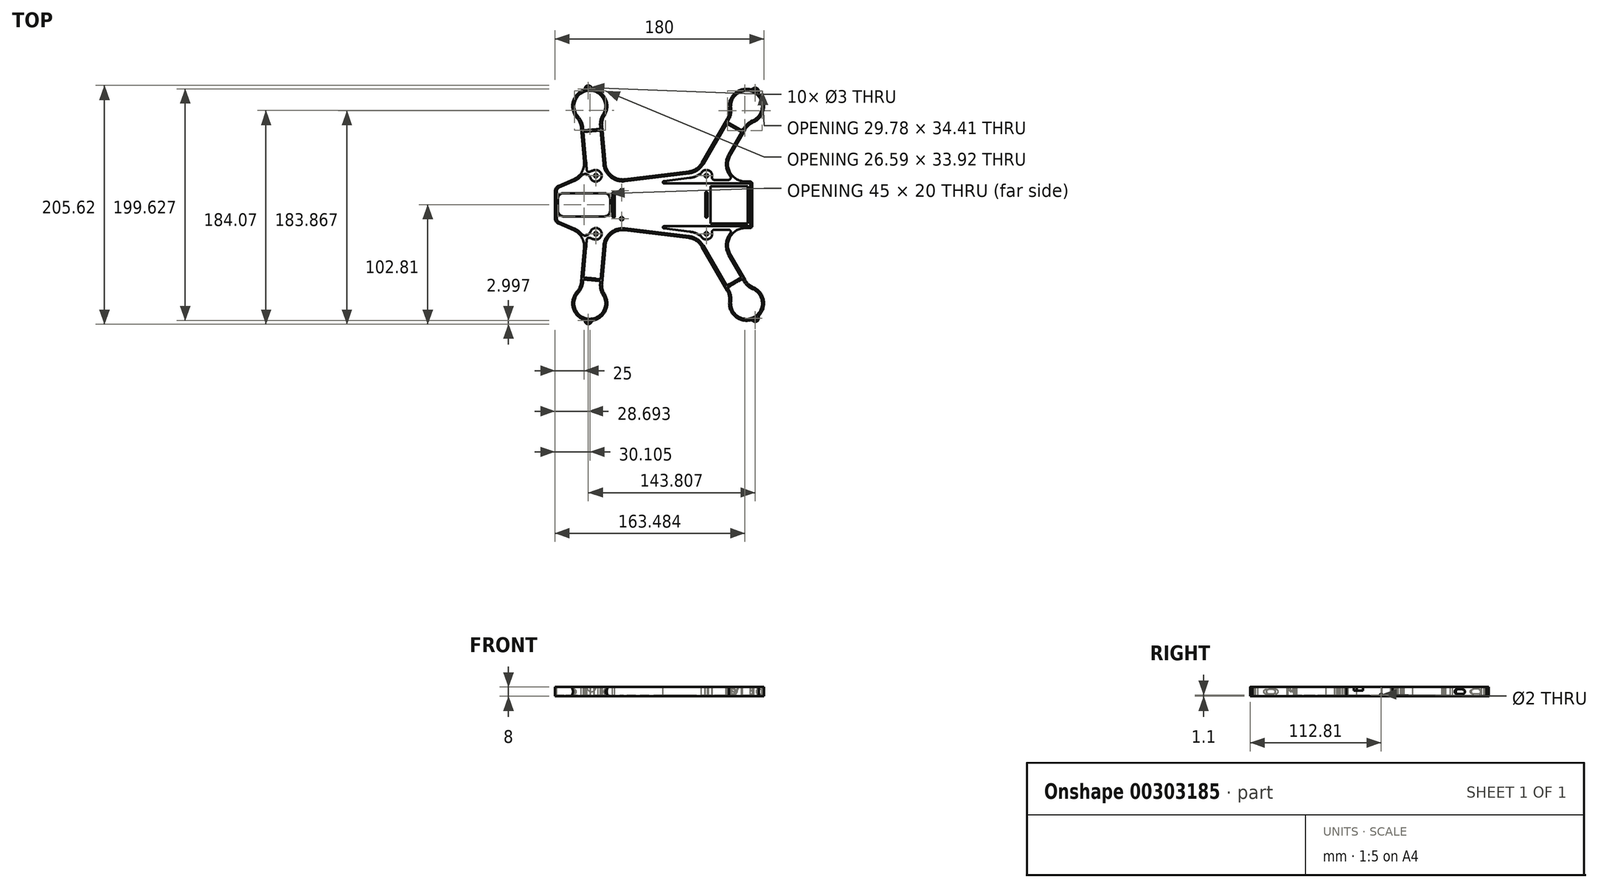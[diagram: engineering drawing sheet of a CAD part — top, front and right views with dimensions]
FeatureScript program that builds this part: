
annotation { "Feature Type Name" : "Feature", "Feature Type Description" : "" }
export const myFeature = defineFeature(function(context is Context, id is Id, definition is map)
    precondition{}
    {
        {
            var Q0;
            Q0=qCreatedBy(makeId("Top.planeOp"),FACE);
            var sketch = newSketch(context, id + "F0", { "sketchPlane" : qUnion([Q0])});
            skLineSegment(sketch, "E0", {"start": v(-85, 0) * mm, "end": v(85, 0) * mm, "construction": true});
            skLineSegment(sketch, "E1", {"start": v(-47.57, 0) * mm, "end": v(-55, -84.87) * mm, "construction": true});
            skLineSegment(sketch, "E2", {"start": v(31, 0) * mm, "end": v(80, -84.87) * mm, "construction": true});
            skArc(sketch, "E3", {"start": v(-66.17, -74.86) * mm, "mid": v(-69.65, -88.1) * mm, "end": v(-60.9, -98.66) * mm});
            skArc(sketch, "E4", {"start": v(65.1, -83.08) * mm, "mid": v(69.86, -95.92) * mm, "end": v(83.07, -99.55) * mm});
            skLineSegment(sketch, "E5", {"start": v(-85, 0) * mm, "end": v(-85, -11.72) * mm});
            skLineSegment(sketch, "E6", {"start": v(-59.85, -37.08) * mm, "end": v(-62.4, -66.15) * mm});
            skLineSegment(sketch, "E7", {"start": v(-44.47, -67.72) * mm, "end": v(-41.64, -35.47) * mm});
            skLineSegment(sketch, "E8", {"start": v(-24.87, -21.9) * mm, "end": v(30.26, -28.66) * mm});
            skLineSegment(sketch, "E9", {"start": v(41.42, -36.05) * mm, "end": v(63.2, -73.78) * mm});
            skLineSegment(sketch, "E10", {"start": v(78.8, -64.78) * mm, "end": v(65.93, -42.5) * mm});
            skLineSegment(sketch, "E11", {"start": v(78.92, -20) * mm, "end": v(83, -20) * mm});
            skLineSegment(sketch, "E12", {"start": v(85, -18) * mm, "end": v(85, 0) * mm});
            skPoint(sketch, "E13.visualSharp", {"position": v(-40.3, -20) * mm});
            skArc(sketch, "E13.filletArc", {"start": v(-24.87, -21.9) * mm, "mid": v(-36.14, -25.12) * mm, "end": v(-41.64, -35.47) * mm});
            skPoint(sketch, "E14.visualSharp", {"position": v(52.94, -20) * mm});
            skPoint(sketch, "E15.visualSharp", {"position": v(37.68, -29.57) * mm});
            skArc(sketch, "E15.filletArc", {"start": v(41.42, -36.05) * mm, "mid": v(36.71, -31.04) * mm, "end": v(30.26, -28.66) * mm});
            skPoint(sketch, "E16.visualSharp", {"position": v(85, -20) * mm});
            skArc(sketch, "E16.filletArc", {"start": v(83, -20) * mm, "mid": v(84.41, -19.41) * mm, "end": v(85, -18) * mm});
            skArc(sketch, "E17.filletArc", {"start": v(78.92, -20) * mm, "mid": v(65.93, -27.5) * mm, "end": v(65.93, -42.5) * mm});
            skPoint(sketch, "E18.visualSharp", {"position": v(-62.92, -72.13) * mm});
            skArc(sketch, "E18.filletArc", {"start": v(-66.17, -74.86) * mm, "mid": v(-63.58, -70.81) * mm, "end": v(-62.4, -66.15) * mm});
            skPoint(sketch, "E19.visualSharp", {"position": v(-44.99, -73.7) * mm});
            skArc(sketch, "E19.filletArc", {"start": v(-44.47, -67.72) * mm, "mid": v(-44.11, -72.52) * mm, "end": v(-42.26, -76.95) * mm});
            skArc(sketch, "E20.filletArc", {"start": v(65.1, -83.08) * mm, "mid": v(64.91, -78.27) * mm, "end": v(63.2, -73.78) * mm});
            skPoint(sketch, "E21.visualSharp", {"position": v(81.8, -69.98) * mm});
            skArc(sketch, "E21.filletArc", {"start": v(78.8, -64.78) * mm, "mid": v(81.83, -68.5) * mm, "end": v(85.9, -71.08) * mm});
            skLineSegment(sketch, "E22", {"start": v(-81.99, -16.3) * mm, "end": v(-68.83, -22) * mm});
            skPoint(sketch, "E23.visualSharp", {"position": v(-85, -15) * mm});
            skArc(sketch, "E23.filletArc", {"start": v(-85, -11.72) * mm, "mid": v(-84.18, -14.46) * mm, "end": v(-81.99, -16.3) * mm});
            skPoint(sketch, "E24.visualSharp", {"position": v(-58.91, -26.3) * mm});
            skArc(sketch, "E25.filletArc", {"start": v(-59.85, -37.08) * mm, "mid": v(-61.9, -28.1) * mm, "end": v(-68.83, -22) * mm});
            skLineSegment(sketch, "E26", {"start": v(78.92, -20) * mm, "end": v(-122.08, -20) * mm, "construction": true});
            skLineSegment(sketch, "E27", {"start": v(-55, -84.87) * mm, "end": v(-57.29, -111.02) * mm, "construction": true});
            skLineSegment(sketch, "E28", {"start": v(80, -84.87) * mm, "end": v(94.45, -109.9) * mm, "construction": true});
            skArc(sketch, "E29.trimOffspring", {"start": v(-51.58, -99.47) * mm, "mid": v(-41.14, -90.6) * mm, "end": v(-42.26, -76.95) * mm});
            skCircle(sketch, "E30", {"center": v(87.5, -97.86) * mm, "radius": 1.5 * mm});
            skArc(sketch, "E31", {"start": v(85.6, -100.18) * mm, "mid": v(89, -100.46) * mm, "end": v(90.46, -97.37) * mm});
            skArc(sketch, "E32.trimOffspring", {"start": v(91.18, -94.87) * mm, "mid": v(94.64, -81.62) * mm, "end": v(85.9, -71.08) * mm});
            skPoint(sketch, "E33.visualSharp", {"position": v(89.94, -96.1) * mm});
            skArc(sketch, "E33.filletArc", {"start": v(91.18, -94.87) * mm, "mid": v(90.54, -96.04) * mm, "end": v(90.46, -97.37) * mm});
            skPoint(sketch, "E34.visualSharp", {"position": v(84.76, -99.1) * mm});
            skArc(sketch, "E35.filletArc", {"start": v(85.6, -100.18) * mm, "mid": v(84.4, -99.58) * mm, "end": v(83.07, -99.55) * mm});
            skCircle(sketch, "E36", {"center": v(-49.76, -25) * mm, "radius": 1.5 * mm});
            skCircle(sketch, "E37", {"center": v(45.43, -25) * mm, "radius": 1.5 * mm});
            skCircle(sketch, "E38", {"center": v(-56.3, -99.81) * mm, "radius": 1.5 * mm});
            skArc(sketch, "E39", {"start": v(-59.2, -100.61) * mm, "mid": v(-56.57, -102.8) * mm, "end": v(-53.6, -101.1) * mm});
            skPoint(sketch, "E40.visualSharp", {"position": v(-53.3, -99.77) * mm});
            skArc(sketch, "E40.filletArc", {"start": v(-51.58, -99.47) * mm, "mid": v(-52.77, -100.06) * mm, "end": v(-53.6, -101.1) * mm});
            skPoint(sketch, "E41.visualSharp", {"position": v(-59.25, -99.25) * mm});
            skArc(sketch, "E41.filletArc", {"start": v(-59.2, -100.61) * mm, "mid": v(-59.83, -99.44) * mm, "end": v(-60.9, -98.66) * mm});
            skLineSegment(sketch, "E42", {"start": v(-55, -84.87) * mm, "end": v(80, -84.87) * mm, "construction": true});
            skLineSegment(sketch, "E43", {"start": v(85, -15) * mm, "end": v(-122.38, -15) * mm, "construction": true});
            skLineSegment(sketch, "E44.2", {"start": v(78.92, -18.4) * mm, "end": v(80, -18.4) * mm});
            skLineSegment(sketch, "E44.4", {"start": v(77.4, -65.58) * mm, "end": v(76.4, -63.85) * mm});
            skArc(sketch, "E44.5", {"start": v(-51.94, -97.92) * mm, "mid": v(-42.62, -90) * mm, "end": v(-43.62, -77.8) * mm});
            skArc(sketch, "E44.8", {"start": v(-64.98, -75.93) * mm, "mid": v(-66.53, -91.7) * mm, "end": v(-51.94, -97.92) * mm});
            skArc(sketch, "E44.9", {"start": v(-64.98, -75.93) * mm, "mid": v(-62.1, -71.45) * mm, "end": v(-60.8, -66.3) * mm});
            skArc(sketch, "E44.15", {"start": v(-46.06, -67.58) * mm, "mid": v(-45.67, -72.89) * mm, "end": v(-43.62, -77.8) * mm});
            skLineSegment(sketch, "E44.16", {"start": v(-46.06, -67.58) * mm, "end": v(-45.89, -65.6) * mm});
            skLineSegment(sketch, "E44.19", {"start": v(30.45, -27.07) * mm, "end": v(30.45, -27.07) * mm});
            skArc(sketch, "E44.21", {"start": v(66.7, -83.27) * mm, "mid": v(66.48, -77.95) * mm, "end": v(64.6, -72.98) * mm});
            skArc(sketch, "E44.22", {"start": v(66.7, -83.27) * mm, "mid": v(74.48, -97.08) * mm, "end": v(89.99, -93.8) * mm});
            skArc(sketch, "E44.25", {"start": v(89.99, -93.8) * mm, "mid": v(93.08, -81.96) * mm, "end": v(85.26, -72.55) * mm});
            skArc(sketch, "E44.26", {"start": v(77.4, -65.58) * mm, "mid": v(80.77, -69.7) * mm, "end": v(85.26, -72.55) * mm});
            skPoint(sketch, "E45.visualSharp", {"position": v(-2, -22.69) * mm});
            skPoint(sketch, "E46.visualSharp", {"position": v(2, -23.18) * mm});
            skLineSegment(sketch, "E47.trimOffspring", {"start": v(-43.24, -35.33) * mm, "end": v(-43.24, -35.33) * mm});
            skLineSegment(sketch, "E48.MirrorCS", {"start": v(78.92, 20) * mm, "end": v(83, 20) * mm});
            skArc(sketch, "E49.MirrorCS", {"start": v(91.18, 94.87) * mm, "mid": v(90.54, 96.04) * mm, "end": v(90.46, 97.37) * mm});
            skLineSegment(sketch, "E50.MirrorCS", {"start": v(78.92, 18.4) * mm, "end": v(80, 18.4) * mm});
            skArc(sketch, "E51.MirrorCS", {"start": v(85.6, 100.18) * mm, "mid": v(84.4, 99.58) * mm, "end": v(83.07, 99.55) * mm});
            skPoint(sketch, "E52.MirrorP", {"position": v(-58.91, 26.3) * mm});
            skPoint(sketch, "E53.MirrorP", {"position": v(52.94, 20) * mm});
            skCircle(sketch, "E54.MirrorC", {"center": v(-56.3, 99.81) * mm, "radius": 1.5 * mm});
            skPoint(sketch, "E55.MirrorP", {"position": v(84.76, 99.1) * mm});
            skArc(sketch, "E56.MirrorCS", {"start": v(-64.98, 75.93) * mm, "mid": v(-62.1, 71.45) * mm, "end": v(-60.8, 66.3) * mm});
            skLineSegment(sketch, "E57.MirrorCS", {"start": v(-44.47, 67.72) * mm, "end": v(-41.64, 35.47) * mm});
            skLineSegment(sketch, "E58.MirrorCS", {"start": v(80, 84.87) * mm, "end": v(94.45, 109.9) * mm, "construction": true});
            skPoint(sketch, "E59.MirrorP", {"position": v(-62.92, 72.13) * mm});
            skPoint(sketch, "E60.MirrorP", {"position": v(-59.25, 99.25) * mm});
            skArc(sketch, "E61.MirrorCS", {"start": v(-24.87, 21.9) * mm, "mid": v(-36.14, 25.12) * mm, "end": v(-41.64, 35.47) * mm});
            skArc(sketch, "E62.MirrorCS", {"start": v(-85, 11.72) * mm, "mid": v(-84.18, 14.46) * mm, "end": v(-81.99, 16.3) * mm});
            skPoint(sketch, "E63.MirrorP", {"position": v(37.68, 29.57) * mm});
            skArc(sketch, "E64.MirrorCS", {"start": v(89.99, 93.8) * mm, "mid": v(93.08, 81.96) * mm, "end": v(85.26, 72.55) * mm});
            skLineSegment(sketch, "E65.MirrorCS", {"start": v(77.4, 65.58) * mm, "end": v(76.4, 63.85) * mm});
            skLineSegment(sketch, "E66.MirrorCS", {"start": v(-24.87, 21.9) * mm, "end": v(30.26, 28.66) * mm});
            skPoint(sketch, "E67.MirrorP", {"position": v(89.94, 96.1) * mm});
            skLineSegment(sketch, "E68.MirrorCS", {"start": v(30.45, 27.07) * mm, "end": v(30.45, 27.07) * mm});
            skCircle(sketch, "E69.MirrorC", {"center": v(45.43, 25) * mm, "radius": 1.5 * mm});
            skCircle(sketch, "E70.MirrorC", {"center": v(87.5, 97.86) * mm, "radius": 1.5 * mm});
            skLineSegment(sketch, "E71.MirrorCS", {"start": v(-55, 84.87) * mm, "end": v(80, 84.87) * mm, "construction": true});
            skArc(sketch, "E72.MirrorCS", {"start": v(-59.2, 100.61) * mm, "mid": v(-56.57, 102.8) * mm, "end": v(-53.6, 101.1) * mm});
            skLineSegment(sketch, "E73.MirrorCS", {"start": v(31, 0) * mm, "end": v(80, 84.87) * mm, "construction": true});
            skArc(sketch, "E74.MirrorCS", {"start": v(-66.17, 74.86) * mm, "mid": v(-63.58, 70.81) * mm, "end": v(-62.4, 66.15) * mm});
            skLineSegment(sketch, "E75.MirrorCS", {"start": v(85, 15) * mm, "end": v(-122.38, 15) * mm, "construction": true});
            skLineSegment(sketch, "E76.MirrorCS", {"start": v(-43.24, 35.33) * mm, "end": v(-43.24, 35.33) * mm});
            skArc(sketch, "E77.MirrorCS", {"start": v(77.4, 65.58) * mm, "mid": v(80.77, 69.7) * mm, "end": v(85.26, 72.55) * mm});
            skPoint(sketch, "E78.MirrorP", {"position": v(-2, 22.69) * mm});
            skArc(sketch, "E79.MirrorCS", {"start": v(-66.17, 74.86) * mm, "mid": v(-69.65, 88.1) * mm, "end": v(-60.9, 98.66) * mm});
            skPoint(sketch, "E80.MirrorP", {"position": v(81.8, 69.98) * mm});
            skLineSegment(sketch, "E81.MirrorCS", {"start": v(-46.06, 67.58) * mm, "end": v(-45.89, 65.6) * mm});
            skArc(sketch, "E82.MirrorCS", {"start": v(78.8, 64.78) * mm, "mid": v(81.83, 68.5) * mm, "end": v(85.9, 71.08) * mm});
            skArc(sketch, "E83.MirrorCS", {"start": v(-59.85, 37.08) * mm, "mid": v(-61.9, 28.1) * mm, "end": v(-68.83, 22) * mm});
            skLineSegment(sketch, "E84.MirrorCS", {"start": v(78.92, 20) * mm, "end": v(-122.08, 20) * mm, "construction": true});
            skArc(sketch, "E85.MirrorCS", {"start": v(66.7, 83.27) * mm, "mid": v(74.48, 97.08) * mm, "end": v(89.99, 93.8) * mm});
            skArc(sketch, "E86.MirrorCS", {"start": v(65.1, 83.08) * mm, "mid": v(69.86, 95.92) * mm, "end": v(83.07, 99.55) * mm});
            skArc(sketch, "E87.MirrorCS", {"start": v(-51.58, 99.47) * mm, "mid": v(-41.14, 90.6) * mm, "end": v(-42.26, 76.95) * mm});
            skPoint(sketch, "E88.MirrorP", {"position": v(-53.3, 99.77) * mm});
            skArc(sketch, "E89.MirrorCS", {"start": v(91.18, 94.87) * mm, "mid": v(94.64, 81.62) * mm, "end": v(85.9, 71.08) * mm});
            skArc(sketch, "E90.MirrorCS", {"start": v(41.42, 36.05) * mm, "mid": v(36.71, 31.04) * mm, "end": v(30.26, 28.66) * mm});
            skArc(sketch, "E91.MirrorCS", {"start": v(-64.98, 75.93) * mm, "mid": v(-66.53, 91.7) * mm, "end": v(-51.94, 97.92) * mm});
            skArc(sketch, "E92.MirrorCS", {"start": v(-51.94, 97.92) * mm, "mid": v(-42.62, 90) * mm, "end": v(-43.62, 77.8) * mm});
            skArc(sketch, "E93.MirrorCS", {"start": v(-44.47, 67.72) * mm, "mid": v(-44.11, 72.52) * mm, "end": v(-42.26, 76.95) * mm});
            skLineSegment(sketch, "E94.MirrorCS", {"start": v(-47.57, 0) * mm, "end": v(-55, 84.87) * mm, "construction": true});
            skLineSegment(sketch, "E95.MirrorCS", {"start": v(78.8, 64.78) * mm, "end": v(65.93, 42.5) * mm});
            skLineSegment(sketch, "E96.MirrorCS", {"start": v(41.42, 36.05) * mm, "end": v(63.2, 73.78) * mm});
            skArc(sketch, "E97.MirrorCS", {"start": v(85.6, 100.18) * mm, "mid": v(89, 100.46) * mm, "end": v(90.46, 97.37) * mm});
            skArc(sketch, "E98.MirrorCS", {"start": v(-46.06, 67.58) * mm, "mid": v(-45.67, 72.89) * mm, "end": v(-43.62, 77.8) * mm});
            skLineSegment(sketch, "E99.MirrorCS", {"start": v(-85, 0) * mm, "end": v(-85, 11.72) * mm});
            skArc(sketch, "E100.MirrorCS", {"start": v(65.1, 83.08) * mm, "mid": v(64.91, 78.27) * mm, "end": v(63.2, 73.78) * mm});
            skArc(sketch, "E101.MirrorCS", {"start": v(78.92, 20) * mm, "mid": v(65.93, 27.5) * mm, "end": v(65.93, 42.5) * mm});
            skArc(sketch, "E102.MirrorCS", {"start": v(66.7, 83.27) * mm, "mid": v(66.48, 77.95) * mm, "end": v(64.6, 72.98) * mm});
            skLineSegment(sketch, "E103.MirrorCS", {"start": v(-55, 84.87) * mm, "end": v(-57.29, 111.02) * mm, "construction": true});
            skPoint(sketch, "E104.MirrorP", {"position": v(-44.99, 73.7) * mm});
            skCircle(sketch, "E105.MirrorC", {"center": v(-49.76, 25) * mm, "radius": 1.5 * mm});
            skPoint(sketch, "E106.MirrorP", {"position": v(-85, 15) * mm});
            skPoint(sketch, "E107.MirrorP", {"position": v(85, 20) * mm});
            skLineSegment(sketch, "E108.MirrorCS", {"start": v(85, 18) * mm, "end": v(85, 0) * mm});
            skArc(sketch, "E109.MirrorCS", {"start": v(83, 20) * mm, "mid": v(84.41, 19.41) * mm, "end": v(85, 18) * mm});
            skPoint(sketch, "E110.MirrorP", {"position": v(-40.3, 20) * mm});
            skLineSegment(sketch, "E111.MirrorCS", {"start": v(-81.99, 16.3) * mm, "end": v(-68.83, 22) * mm});
            skLineSegment(sketch, "E112.MirrorCS", {"start": v(-59.85, 37.08) * mm, "end": v(-62.4, 66.15) * mm});
            skPoint(sketch, "E113.MirrorP", {"position": v(2, 23.18) * mm});
            skArc(sketch, "E114.filletArc", {"start": v(-60.9, 98.66) * mm, "mid": v(-59.83, 99.44) * mm, "end": v(-59.2, 100.61) * mm});
            skArc(sketch, "E115.filletArc", {"start": v(-53.6, 101.1) * mm, "mid": v(-52.77, 100.06) * mm, "end": v(-51.58, 99.47) * mm});
            skLineSegment(sketch, "E116", {"start": v(-60.63, -64.3) * mm, "end": v(-45.89, -65.6) * mm});
            skLineSegment(sketch, "E117.trimOffspring", {"start": v(-60.63, -64.3) * mm, "end": v(-60.8, -66.3) * mm});
            skLineSegment(sketch, "E118", {"start": v(63.6, -71.25) * mm, "end": v(76.4, -63.85) * mm});
            skLineSegment(sketch, "E119.trimOffspring", {"start": v(63.6, -71.25) * mm, "end": v(64.6, -72.98) * mm});
            skLineSegment(sketch, "E120.MirrorCS", {"start": v(-60.63, 64.3) * mm, "end": v(-45.89, 65.6) * mm});
            skLineSegment(sketch, "E121.MirrorCS", {"start": v(63.6, 71.25) * mm, "end": v(76.4, 63.85) * mm});
            skLineSegment(sketch, "E122.trimOffspring", {"start": v(63.6, 71.25) * mm, "end": v(64.6, 72.98) * mm});
            skLineSegment(sketch, "E123.trimOffspring", {"start": v(-60.63, 64.3) * mm, "end": v(-60.8, 66.3) * mm});
            skCircle(sketch, "E124", {"center": v(0, 0) * mm, "radius": 134.27 * mm, "construction": true});
            skLineSegment(sketch, "E125.bottom", {"start": v(-42.5, -10) * mm, "end": v(-77.5, -10) * mm});
            skLineSegment(sketch, "E125.top", {"start": v(-42.5, 10) * mm, "end": v(-77.5, 10) * mm});
            skLineSegment(sketch, "E125.left", {"start": v(-37.5, -5) * mm, "end": v(-37.5, 5) * mm});
            skLineSegment(sketch, "E125.right", {"start": v(-82.5, -5) * mm, "end": v(-82.5, 5) * mm});
            skArc(sketch, "E126.filletArc", {"start": v(-37.5, 5) * mm, "mid": v(-38.96, 8.54) * mm, "end": v(-42.5, 10) * mm});
            skArc(sketch, "E127.filletArc", {"start": v(-82.5, -5) * mm, "mid": v(-81.04, -8.54) * mm, "end": v(-77.5, -10) * mm});
            skArc(sketch, "E128.filletArc", {"start": v(-77.5, 10) * mm, "mid": v(-81.04, 8.54) * mm, "end": v(-82.5, 5) * mm});
            skArc(sketch, "E129.filletArc", {"start": v(-42.5, -10) * mm, "mid": v(-38.96, -8.54) * mm, "end": v(-37.5, -5) * mm});
            skCircle(sketch, "E130", {"center": v(-27.5, -12) * mm, "radius": 1.5 * mm});
            skCircle(sketch, "E131.MirrorC", {"center": v(-27.5, 12) * mm, "radius": 1.5 * mm});
            skSolve(sketch);
        }
        {
            var Q0;
            Q0=makeQuery(id+"F0.imprint","IMPRINT",FACE,{"disambiguationData":[TD([[makeQuery(id+"F0.imprint","IMPRINT",EDGE,{"derivedFrom":sQuery(id+"F0.wireOp",EDGE,"E3")}),1.0]])]});
            extrude(context, id + "F1", {"entities" : qUnion([Q0]), "depth" : 8 * mm});
        }
        {
            var Q0;
            Q0=makeQuery(id+"F1.opExtrude","CAP_FACE",FACE,{"disambiguationData":[OSD([sQuery(id+"F0.wireOp",EDGE,"E3"),sQuery(id+"F0.wireOp",EDGE,"E4"),sQuery(id+"F0.wireOp",EDGE,"E5"),sQuery(id+"F0.wireOp",EDGE,"E6"),sQuery(id+"F0.wireOp",EDGE,"E7"),sQuery(id+"F0.wireOp",EDGE,"E8"),sQuery(id+"F0.wireOp",EDGE,"E9"),sQuery(id+"F0.wireOp",EDGE,"E10"),sQuery(id+"F0.wireOp",EDGE,"E11"),sQuery(id+"F0.wireOp",EDGE,"E12"),sQuery(id+"F0.wireOp",EDGE,"E13.filletArc"),sQuery(id+"F0.wireOp",EDGE,"E15.filletArc"),sQuery(id+"F0.wireOp",EDGE,"E16.filletArc"),sQuery(id+"F0.wireOp",EDGE,"E17.filletArc"),sQuery(id+"F0.wireOp",EDGE,"E18.filletArc"),sQuery(id+"F0.wireOp",EDGE,"E19.filletArc"),sQuery(id+"F0.wireOp",EDGE,"E20.filletArc"),sQuery(id+"F0.wireOp",EDGE,"E21.filletArc"),sQuery(id+"F0.wireOp",EDGE,"E22"),sQuery(id+"F0.wireOp",EDGE,"E23.filletArc"),sQuery(id+"F0.wireOp",EDGE,"E25.filletArc"),sQuery(id+"F0.wireOp",EDGE,"E29.trimOffspring"),sQuery(id+"F0.wireOp",EDGE,"E30"),sQuery(id+"F0.wireOp",EDGE,"E31"),sQuery(id+"F0.wireOp",EDGE,"E32.trimOffspring"),sQuery(id+"F0.wireOp",EDGE,"E33.filletArc"),sQuery(id+"F0.wireOp",EDGE,"E35.filletArc"),sQuery(id+"F0.wireOp",EDGE,"E36"),sQuery(id+"F0.wireOp",EDGE,"E37"),sQuery(id+"F0.wireOp",EDGE,"E38"),sQuery(id+"F0.wireOp",EDGE,"E39"),sQuery(id+"F0.wireOp",EDGE,"E40.filletArc"),sQuery(id+"F0.wireOp",EDGE,"E41.filletArc"),sQuery(id+"F0.wireOp",EDGE,"E44.4"),sQuery(id+"F0.wireOp",EDGE,"E44.5"),sQuery(id+"F0.wireOp",EDGE,"E44.8"),sQuery(id+"F0.wireOp",EDGE,"E44.9"),sQuery(id+"F0.wireOp",EDGE,"E44.10"),sQuery(id+"F0.wireOp",EDGE,"E44.11"),sQuery(id+"F0.wireOp",EDGE,"E44.12"),sQuery(id+"F0.wireOp",EDGE,"E44.13"),sQuery(id+"F0.wireOp",EDGE,"E44.15"),sQuery(id+"F0.wireOp",EDGE,"E44.16"),sQuery(id+"F0.wireOp",EDGE,"E44.20"),sQuery(id+"F0.wireOp",EDGE,"E44.21"),sQuery(id+"F0.wireOp",EDGE,"E44.22"),sQuery(id+"F0.wireOp",EDGE,"E44.25"),sQuery(id+"F0.wireOp",EDGE,"E44.26"),sQuery(id+"F0.wireOp",EDGE,"55a75c94-3981-4925-938c-0703a2540f2a"),sQuery(id+"F0.wireOp",EDGE,"18e9a88f-63d2-484e-94f8-6aafb132c643"),sQuery(id+"F0.wireOp",EDGE,"3e357946-6a65-48ba-9413-4c9084a4b4eb"),sQuery(id+"F0.wireOp",EDGE,"9b53bd53-ce0e-4c03-85f3-8b744b70c49f.trimOffspring"),sQuery(id+"F0.wireOp",EDGE,"E48.MirrorCS"),sQuery(id+"F0.wireOp",EDGE,"E49.MirrorCS"),sQuery(id+"F0.wireOp",EDGE,"E51.MirrorCS"),sQuery(id+"F0.wireOp",EDGE,"E54.MirrorC"),sQuery(id+"F0.wireOp",EDGE,"E56.MirrorCS"),sQuery(id+"F0.wireOp",EDGE,"E57.MirrorCS"),sQuery(id+"F0.wireOp",EDGE,"E61.MirrorCS"),sQuery(id+"F0.wireOp",EDGE,"E62.MirrorCS"),sQuery(id+"F0.wireOp",EDGE,"E64.MirrorCS"),sQuery(id+"F0.wireOp",EDGE,"E65.MirrorCS"),sQuery(id+"F0.wireOp",EDGE,"E66.MirrorCS"),sQuery(id+"F0.wireOp",EDGE,"E69.MirrorC"),sQuery(id+"F0.wireOp",EDGE,"E508.MirrorCS"),sQuery(id+"F0.wireOp",EDGE,"E70.MirrorC"),sQuery(id+"F0.wireOp",EDGE,"7aa77c07-5236-4930-a80c-88c67a00b59931.MirrorCS"),sQuery(id+"F0.wireOp",EDGE,"E72.MirrorCS"),sQuery(id+"F0.wireOp",EDGE,"E74.MirrorCS"),sQuery(id+"F0.wireOp",EDGE,"7aa77c07-5236-4930-a80c-88c67a00b59935.MirrorCS"),sQuery(id+"F0.wireOp",EDGE,"7aa77c07-5236-4930-a80c-88c67a00b59937.MirrorCS"),sQuery(id+"F0.wireOp",EDGE,"E77.MirrorCS"),sQuery(id+"F0.wireOp",EDGE,"E79.MirrorCS"),sQuery(id+"F0.wireOp",EDGE,"E81.MirrorCS"),sQuery(id+"F0.wireOp",EDGE,"E82.MirrorCS"),sQuery(id+"F0.wireOp",EDGE,"E83.MirrorCS"),sQuery(id+"F0.wireOp",EDGE,"E85.MirrorCS"),sQuery(id+"F0.wireOp",EDGE,"E86.MirrorCS"),sQuery(id+"F0.wireOp",EDGE,"E87.MirrorCS"),sQuery(id+"F0.wireOp",EDGE,"E89.MirrorCS"),sQuery(id+"F0.wireOp",EDGE,"E90.MirrorCS"),sQuery(id+"F0.wireOp",EDGE,"E91.MirrorCS"),sQuery(id+"F0.wireOp",EDGE,"E92.MirrorCS"),sQuery(id+"F0.wireOp",EDGE,"E93.MirrorCS"),sQuery(id+"F0.wireOp",EDGE,"E95.MirrorCS"),sQuery(id+"F0.wireOp",EDGE,"E96.MirrorCS"),sQuery(id+"F0.wireOp",EDGE,"E97.MirrorCS"),sQuery(id+"F0.wireOp",EDGE,"E98.MirrorCS"),sQuery(id+"F0.wireOp",EDGE,"E99.MirrorCS"),sQuery(id+"F0.wireOp",EDGE,"E100.MirrorCS"),sQuery(id+"F0.wireOp",EDGE,"E101.MirrorCS"),sQuery(id+"F0.wireOp",EDGE,"E102.MirrorCS"),sQuery(id+"F0.wireOp",EDGE,"7aa77c07-5236-4930-a80c-88c67a00b59970.MirrorCS"),sQuery(id+"F0.wireOp",EDGE,"E105.MirrorC"),sQuery(id+"F0.wireOp",EDGE,"7aa77c07-5236-4930-a80c-88c67a00b59978.MirrorCS"),sQuery(id+"F0.wireOp",EDGE,"7aa77c07-5236-4930-a80c-88c67a00b59979.MirrorCS"),sQuery(id+"F0.wireOp",EDGE,"E530.MirrorCS"),sQuery(id+"F0.wireOp",EDGE,"E108.MirrorCS"),sQuery(id+"F0.wireOp",EDGE,"E109.MirrorCS"),sQuery(id+"F0.wireOp",EDGE,"E111.MirrorCS"),sQuery(id+"F0.wireOp",EDGE,"E112.MirrorCS"),sQuery(id+"F0.wireOp",EDGE,"E537.MirrorCS"),sQuery(id+"F0.wireOp",EDGE,"E114.filletArc"),sQuery(id+"F0.wireOp",EDGE,"E115.filletArc"),sQuery(id+"F0.wireOp",EDGE,"a4d90b42-d63e-410f-917a-941b09824992"),sQuery(id+"F0.wireOp",EDGE,"E116"),sQuery(id+"F0.wireOp",EDGE,"cMJuFud1-vg0K-iN1q-p5d7-nlo64yB5XbXq"),sQuery(id+"F0.wireOp",EDGE,"E117.trimOffspring"),sQuery(id+"F0.wireOp",EDGE,"74f08385-9b30-422e-95e3-7c0d5ab4f87f.trimOffspring"),sQuery(id+"F0.wireOp",EDGE,"E118"),sQuery(id+"F0.wireOp",EDGE,"s3oDME9j-RjMK-g1Hw-ZGjj-mhpWrOwCSelL"),sQuery(id+"F0.wireOp",EDGE,"b3e49e08-c0df-423a-bc82-550474e4bf9f.trimOffspring"),sQuery(id+"F0.wireOp",EDGE,"E119.trimOffspring"),sQuery(id+"F0.wireOp",EDGE,"31413146-a01f-4e31-a23e-b78ac6f1261a0.MirrorCS"),sQuery(id+"F0.wireOp",EDGE,"E120.MirrorCS"),sQuery(id+"F0.wireOp",EDGE,"14c246ef-2517-462f-98e1-722c737d70360.MirrorCS"),sQuery(id+"F0.wireOp",EDGE,"E121.MirrorCS"),sQuery(id+"F0.wireOp",EDGE,"35ee15a8-cd36-4e2e-a5d4-a9be4718c77d.trimOffspring"),sQuery(id+"F0.wireOp",EDGE,"E122.trimOffspring"),sQuery(id+"F0.wireOp",EDGE,"3fd240ab-1996-4fb1-8bde-4f594ce2e648.trimOffspring"),sQuery(id+"F0.wireOp",EDGE,"E123.trimOffspring")])],"isStart":false});
            var sketch = newSketch(context, id + "F2", { "sketchPlane" : qUnion([Q0])});
            skLineSegment(sketch, "E132.MirrorCS", {"start": v(78.92, 18.4) * mm, "end": v(78.92, 18.4) * mm});
            skLineSegment(sketch, "E133", {"start": v(78.92, -18.4) * mm, "end": v(8.98, -18.4) * mm});
            skLineSegment(sketch, "E134", {"start": v(78.92, -18.4) * mm, "end": v(-100.25, -18.4) * mm, "construction": true});
            skPoint(sketch, "E135", {"position": v(45.4, -10) * mm});
            skPoint(sketch, "E136", {"position": v(45.4, 10) * mm});
            skLineSegment(sketch, "E137", {"start": v(45.4, 10) * mm, "end": v(45.4, -10) * mm, "construction": true});
            skArc(sketch, "E138.0.startCap", {"start": v(44.4, 10) * mm, "mid": v(45.4, 11) * mm, "end": v(46.4, 10) * mm});
            skArc(sketch, "E138.0.endCap", {"start": v(46.4, -10) * mm, "mid": v(45.4, -11) * mm, "end": v(44.4, -10) * mm});
            skLineSegment(sketch, "E138.0.left", {"start": v(46.4, 10) * mm, "end": v(46.4, -10) * mm});
            skLineSegment(sketch, "E138.0.right", {"start": v(44.4, 10) * mm, "end": v(44.4, -10) * mm});
            skLineSegment(sketch, "E139.2.0.0", {"start": v(-35.4, 10) * mm, "end": v(-35.4, -10) * mm});
            skLineSegment(sketch, "E139.2.0.1", {"start": v(-33.4, 10) * mm, "end": v(-33.4, -10) * mm});
            skArc(sketch, "E139.2.0.2", {"start": v(-35.4, 10) * mm, "mid": v(-34.4, 11) * mm, "end": v(-33.4, 10) * mm});
            skArc(sketch, "E139.2.0.3", {"start": v(-33.4, -10) * mm, "mid": v(-34.4, -11) * mm, "end": v(-35.4, -10) * mm});
            skLineSegment(sketch, "E140.0", {"start": v(83, 18.4) * mm, "end": v(78.92, 18.4) * mm});
            skArc(sketch, "E140.1", {"start": v(83.4, 18) * mm, "mid": v(83.28, 18.28) * mm, "end": v(83, 18.4) * mm});
            skLineSegment(sketch, "E140.2", {"start": v(83.4, -18) * mm, "end": v(83.4, 18) * mm});
            skArc(sketch, "E140.3", {"start": v(83, -18.4) * mm, "mid": v(83.28, -18.28) * mm, "end": v(83.4, -18) * mm});
            skLineSegment(sketch, "E140.4", {"start": v(78.92, -18.4) * mm, "end": v(83, -18.4) * mm});
            skArc(sketch, "E140.5", {"start": v(64.54, -43.3) * mm, "mid": v(62.37, -33.76) * mm, "end": v(65.94, -24.65) * mm});
            skLineSegment(sketch, "E140.6", {"start": v(75.6, -62.46) * mm, "end": v(64.54, -43.3) * mm});
            skLineSegment(sketch, "E140.10", {"start": v(-60.49, 62.7) * mm, "end": v(-58.26, 37.22) * mm});
            skLineSegment(sketch, "E140.18", {"start": v(-43.24, 35.33) * mm, "end": v(-45.75, 64) * mm});
            skArc(sketch, "E140.19", {"start": v(-24.68, 20.3) * mm, "mid": v(-37.15, 23.88) * mm, "end": v(-43.24, 35.33) * mm});
            skLineSegment(sketch, "E140.20", {"start": v(30.45, 27.07) * mm, "end": v(-24.68, 20.3) * mm});
            skArc(sketch, "E140.21", {"start": v(42.8, 35.25) * mm, "mid": v(37.6, 29.7) * mm, "end": v(30.45, 27.07) * mm});
            skLineSegment(sketch, "E140.24", {"start": v(64.54, 43.3) * mm, "end": v(75.6, 62.46) * mm});
            skArc(sketch, "E140.25", {"start": v(65.94, 24.65) * mm, "mid": v(62.37, 33.76) * mm, "end": v(64.54, 43.3) * mm});
            skLineSegment(sketch, "E140.31", {"start": v(62.8, 69.86) * mm, "end": v(42.8, 35.25) * mm});
            skArc(sketch, "E140.32", {"start": v(-62.33, 24.81) * mm, "mid": v(-65.02, 22.35) * mm, "end": v(-68.2, 20.54) * mm});
            skLineSegment(sketch, "E140.33", {"start": v(-68.2, 20.54) * mm, "end": v(-81.35, 14.84) * mm});
            skArc(sketch, "E140.34", {"start": v(-81.35, 14.84) * mm, "mid": v(-82.84, 13.58) * mm, "end": v(-83.4, 11.72) * mm});
            skLineSegment(sketch, "E140.35", {"start": v(-83.4, 11.72) * mm, "end": v(-83.4, -11.72) * mm});
            skArc(sketch, "E140.36", {"start": v(-83.4, -11.72) * mm, "mid": v(-82.84, -13.58) * mm, "end": v(-81.35, -14.84) * mm});
            skLineSegment(sketch, "E140.37", {"start": v(-81.35, -14.84) * mm, "end": v(-68.2, -20.54) * mm});
            skArc(sketch, "E140.38", {"start": v(-68.2, -20.54) * mm, "mid": v(-65.02, -22.35) * mm, "end": v(-62.33, -24.81) * mm});
            skLineSegment(sketch, "E140.39", {"start": v(-58.26, -37.22) * mm, "end": v(-60.49, -62.7) * mm});
            skLineSegment(sketch, "E140.47", {"start": v(-45.75, -64) * mm, "end": v(-43.24, -35.33) * mm});
            skArc(sketch, "E140.48", {"start": v(-43.24, -35.33) * mm, "mid": v(-37.15, -23.88) * mm, "end": v(-24.68, -20.3) * mm});
            skLineSegment(sketch, "E140.49", {"start": v(-24.68, -20.3) * mm, "end": v(30.45, -27.07) * mm});
            skArc(sketch, "E140.50", {"start": v(30.45, -27.07) * mm, "mid": v(37.6, -29.7) * mm, "end": v(42.8, -35.25) * mm});
            skLineSegment(sketch, "E140.51", {"start": v(42.8, -35.25) * mm, "end": v(62.8, -69.86) * mm});
            skLineSegment(sketch, "E141", {"start": v(-60.49, -62.7) * mm, "end": v(-45.75, -64) * mm});
            skLineSegment(sketch, "E142", {"start": v(62.8, -69.86) * mm, "end": v(75.6, -62.46) * mm});
            skArc(sketch, "E143", {"start": v(-51.36, -29.74) * mm, "mid": v(-45.17, -23.02) * mm, "end": v(-54.3, -22.9) * mm});
            skArc(sketch, "E144", {"start": v(40.93, -27.18) * mm, "mid": v(47.1, -29.71) * mm, "end": v(50.3, -23.86) * mm});
            skLineSegment(sketch, "E145", {"start": v(64.38, -21.4) * mm, "end": v(52.25, -21.4) * mm});
            skArc(sketch, "E146.0", {"start": v(30.94, -23.1) * mm, "mid": v(36.2, -24.48) * mm, "end": v(40.93, -27.18) * mm});
            skLineSegment(sketch, "E146.1", {"start": v(8.86, -20.4) * mm, "end": v(30.94, -23.1) * mm});
            skPoint(sketch, "E147.visualSharp", {"position": v(48.9, -21.4) * mm});
            skArc(sketch, "E147.filletArc", {"start": v(52.25, -21.4) * mm, "mid": v(50.68, -22.16) * mm, "end": v(50.3, -23.86) * mm});
            skPoint(sketch, "E148.visualSharp", {"position": v(69.4, -21.4) * mm});
            skArc(sketch, "E148.filletArc", {"start": v(65.94, -24.65) * mm, "mid": v(66.18, -22.53) * mm, "end": v(64.38, -21.4) * mm});
            skPoint(sketch, "E149.visualSharp", {"position": v(-7.37, -18.4) * mm});
            skArc(sketch, "E149.filletArc", {"start": v(8.98, -18.4) * mm, "mid": v(7.98, -19.34) * mm, "end": v(8.86, -20.4) * mm});
            skFitSpline(sketch, "E150", {"points": [v(-62.55, -24.56) * mm, v(-57.79, -26.4) * mm, v(-54.3, -22.9) * mm], "startDerivative": vector(11.1, -12.78) * mm, "endDerivative": vector(6.86, 13.68) * mm});
            skFitSpline(sketch, "E151", {"points": [v(-58.26, -37.22) * mm, v(-56.74, -28.54) * mm, v(-51.36, -29.74) * mm], "startDerivative": vector(2.7, 21.07) * mm, "endDerivative": vector(15.18, -3.9) * mm});
            skLineSegment(sketch, "E152.MirrorCS", {"start": v(78.92, 18.4) * mm, "end": v(8.98, 18.4) * mm});
            skArc(sketch, "E153.MirrorCS", {"start": v(65.94, 24.65) * mm, "mid": v(66.18, 22.53) * mm, "end": v(64.38, 21.4) * mm});
            skLineSegment(sketch, "E154.MirrorCS", {"start": v(8.86, 20.4) * mm, "end": v(30.94, 23.1) * mm});
            skLineSegment(sketch, "E155.MirrorCS", {"start": v(64.38, 21.4) * mm, "end": v(52.25, 21.4) * mm});
            skArc(sketch, "E156.MirrorCS", {"start": v(52.25, 21.4) * mm, "mid": v(50.68, 22.16) * mm, "end": v(50.3, 23.86) * mm});
            skArc(sketch, "E157.MirrorCS", {"start": v(40.93, 27.18) * mm, "mid": v(47.1, 29.71) * mm, "end": v(50.3, 23.86) * mm});
            skArc(sketch, "E158.MirrorCS", {"start": v(30.94, 23.1) * mm, "mid": v(36.2, 24.48) * mm, "end": v(40.93, 27.18) * mm});
            skArc(sketch, "E159.MirrorCS", {"start": v(8.98, 18.4) * mm, "mid": v(7.98, 19.34) * mm, "end": v(8.86, 20.4) * mm});
            skArc(sketch, "E160.MirrorCS", {"start": v(-51.36, 29.74) * mm, "mid": v(-45.17, 23.02) * mm, "end": v(-54.3, 22.9) * mm});
            skFitSpline(sketch, "E161.MirrorCS", {"points": [v(-58.26, 37.22) * mm, v(-56.74, 28.54) * mm, v(-51.36, 29.74) * mm], "startDerivative": vector(2.7, -21.07) * mm, "endDerivative": vector(15.18, 3.9) * mm});
            skFitSpline(sketch, "E162.MirrorCS", {"points": [v(-62.55, 24.56) * mm, v(-57.79, 26.4) * mm, v(-54.3, 22.9) * mm], "startDerivative": vector(11.1, 12.78) * mm, "endDerivative": vector(6.86, -13.68) * mm});
            skLineSegment(sketch, "E163.MirrorCS", {"start": v(62.8, 69.86) * mm, "end": v(75.6, 62.46) * mm});
            skLineSegment(sketch, "E164.MirrorCS", {"start": v(-60.49, 62.7) * mm, "end": v(-45.75, 64) * mm});
            skSolve(sketch);
        }
        {
            var Q0;
            Q0=makeQuery(id+"F2.imprint","IMPRINT",FACE,{"disambiguationData":[TD([[makeQuery(id+"F2.imprint","IMPRINT",EDGE,{"derivedFrom":sQuery(id+"F2.wireOp",EDGE,"E133")}),-1.0]])]});
            extrude(context, id + "F3", {"entities" : qUnion([Q0]), "operationType" : NewBodyOperationType.REMOVE, "oppositeDirection" : true, "depth" : 7.4 * mm});
        }
        {
            var Q0;
            Q0=makeQuery(id+"F1.opExtrude","SWEPT_FACE",FACE,{"disambiguationData":[OSD([sQuery(id+"F0.wireOp",EDGE,"E12"),sQuery(id+"F0.wireOp",EDGE,"E108.MirrorCS")])]});
            var sketch = newSketch(context, id + "F4", { "sketchPlane" : qUnion([Q0])});
            skLineSegment(sketch, "E165.bottom", {"start": v(-13.5, 8) * mm, "end": v(-5.5, 8) * mm});
            skLineSegment(sketch, "E165.top", {"start": v(-13.5, 5) * mm, "end": v(-5.5, 5) * mm});
            skLineSegment(sketch, "E165.left", {"start": v(-13.5, 8) * mm, "end": v(-13.5, 5) * mm});
            skLineSegment(sketch, "E165.right", {"start": v(-5.5, 8) * mm, "end": v(-5.5, 5) * mm});
            skCircle(sketch, "E166", {"center": v(10, 1.1) * mm, "radius": 1 * mm});
            skSolve(sketch);
        }
        {
            var Q0;
            Q0=makeQuery(id+"F4.imprint","IMPRINT",FACE,{"disambiguationData":[TD([[makeQuery(id+"F4.imprint","IMPRINT",EDGE,{"derivedFrom":sQuery(id+"F4.wireOp",EDGE,"E165.bottom")}),-1.0]])]});
            var Q1;
            Q1=makeQuery(id+"F4.imprint","IMPRINT",FACE,{"disambiguationData":[TD([[makeQuery(id+"F4.imprint","IMPRINT",EDGE,{"derivedFrom":sQuery(id+"F4.wireOp",EDGE,"E166")}),1.0]])]});
            extrude(context, id + "F5", {"entities" : qUnion([Q0, Q1]), "operationType" : NewBodyOperationType.REMOVE, "oppositeDirection" : true, "depth" : 4 * mm});
        }
        {
            var Q0;
            Q0=makeQuery(id+"F3.boolean.opBoolean","COPY",FACE,{"derivedFrom":makeQuery(id+"F3.opExtrude","CAP_FACE",FACE,{"disambiguationData":[OSD([sQuery(id+"F0.wireOp",EDGE,"55a75c94-3981-4925-938c-0703a2540f2a"),sQuery(id+"F0.wireOp",EDGE,"18e9a88f-63d2-484e-94f8-6aafb132c643"),sQuery(id+"F0.wireOp",EDGE,"3e357946-6a65-48ba-9413-4c9084a4b4eb"),sQuery(id+"F0.wireOp",EDGE,"7aa77c07-5236-4930-a80c-88c67a00b59935.MirrorCS"),sQuery(id+"F0.wireOp",EDGE,"7aa77c07-5236-4930-a80c-88c67a00b59978.MirrorCS"),sQuery(id+"F0.wireOp",EDGE,"7aa77c07-5236-4930-a80c-88c67a00b59979.MirrorCS"),sQuery(id+"F0.wireOp",EDGE,"a4d90b42-d63e-410f-917a-941b09824992"),sQuery(id+"F2.wireOp",EDGE,"fffe1e67-2cc9-48c4-8983-8611bc80b19c.0"),sQuery(id+"F2.wireOp",EDGE,"fffe1e67-2cc9-48c4-8983-8611bc80b19c.1"),sQuery(id+"F2.wireOp",EDGE,"fffe1e67-2cc9-48c4-8983-8611bc80b19c.2"),sQuery(id+"F2.wireOp",EDGE,"2246689b-3c9b-4c8e-905d-07fedf87c73f.2"),sQuery(id+"F2.wireOp",EDGE,"d914186b-a5e1-4f1c-b080-cd34f5ce877f0.MirrorCS"),sQuery(id+"F2.wireOp",EDGE,"5fff3e55-b558-4c72-8411-46350b7e51440.MirrorCS"),sQuery(id+"F2.wireOp",EDGE,"5c2eff44-0bb9-47c2-831a-ff12a0e9dea30.MirrorCS"),sQuery(id+"F2.wireOp",EDGE,"a0e3ad08-1fbb-4ff4-acfc-af0f5074732f0.MirrorCS"),sQuery(id+"F2.wireOp",EDGE,"YLonHyPl-4aFv-fIO4-gWat-4KreMwAxru9C"),sQuery(id+"F2.wireOp",EDGE,"E133"),sQuery(id+"F2.wireOp",EDGE,"f0677aad-6ccf-4ac1-86a8-1c334f34c33b0.MirrorCS"),sQuery(id+"F2.wireOp",EDGE,"0db9f0e9-9e14-4ac0-91a2-759e6fbd4fb7.2.left"),sQuery(id+"F2.wireOp",EDGE,"abe0898a-1f7c-4316-9df3-18db7f33bf87"),sQuery(id+"F2.wireOp",EDGE,"20a845a6-1cc5-41a5-8aa5-076ad581321a"),sQuery(id+"F2.wireOp",EDGE,"50eb1c94-5ace-404b-bcef-2d3eae4a823a.filletArc"),sQuery(id+"F2.wireOp",EDGE,"05c023b2-4da7-4de4-8dc0-9080a339fc651.MirrorCS"),sQuery(id+"F2.wireOp",EDGE,"05c023b2-4da7-4de4-8dc0-9080a339fc657.MirrorCS"),sQuery(id+"F2.wireOp",EDGE,"05c023b2-4da7-4de4-8dc0-9080a339fc658.MirrorCS"),sQuery(id+"F2.wireOp",EDGE,"05c023b2-4da7-4de4-8dc0-9080a339fc659.MirrorCS"),sQuery(id+"F2.wireOp",EDGE,"0ITbmxvW-dEQf-i5GW-sRUa-ICrX6OYGrSRM"),sQuery(id+"F2.wireOp",EDGE,"81397a56-36e4-4d1a-aac4-778d4ba0b91e0.MirrorCS"),sQuery(id+"F2.wireOp",EDGE,"08d4352a-0a2f-4740-9c2c-cdb5e3f0d8b7.trimOffspring"),sQuery(id+"F2.wireOp",EDGE,"e74299a3-ef13-446a-a17a-9097ae4e11bd.trimOffspring"),sQuery(id+"F2.wireOp",EDGE,"ce151ea7-cdd1-498e-a54c-a8153daecff6.trimOffspring"),sQuery(id+"F2.wireOp",EDGE,"96f9a0b3-2fe5-4509-b9fd-21347e342cb5.trimOffspring"),sQuery(id+"F2.wireOp",EDGE,"E138.0.startCap"),sQuery(id+"F2.wireOp",EDGE,"E138.0.endCap"),sQuery(id+"F2.wireOp",EDGE,"E138.0.left"),sQuery(id+"F2.wireOp",EDGE,"E138.0.right"),sQuery(id+"F2.wireOp",EDGE,"E139.1.0.0"),sQuery(id+"F2.wireOp",EDGE,"E139.1.0.1"),sQuery(id+"F2.wireOp",EDGE,"E139.1.0.2"),sQuery(id+"F2.wireOp",EDGE,"E139.1.0.3"),sQuery(id+"F2.wireOp",EDGE,"E139.2.0.0"),sQuery(id+"F2.wireOp",EDGE,"E139.2.0.1"),sQuery(id+"F2.wireOp",EDGE,"E139.2.0.2"),sQuery(id+"F2.wireOp",EDGE,"E139.2.0.3")])],"isStart":false})});
            var sketch = newSketch(context, id + "F6", { "sketchPlane" : qUnion([Q0])});
            skLineSegment(sketch, "E167.bottom", {"start": v(49, 16) * mm, "end": v(81, 16) * mm});
            skLineSegment(sketch, "E167.top", {"start": v(49, -16) * mm, "end": v(81, -16) * mm});
            skLineSegment(sketch, "E167.left", {"start": v(49, 16) * mm, "end": v(49, -16) * mm});
            skLineSegment(sketch, "E167.right", {"start": v(81, 16) * mm, "end": v(81, -16) * mm});
            skSolve(sketch);
        }
        {
            var Q0;
            Q0=makeQuery(id+"F6.imprint","IMPRINT",FACE,{"disambiguationData":[TD([[makeQuery(id+"F6.imprint","IMPRINT",EDGE,{"derivedFrom":sQuery(id+"F6.wireOp",EDGE,"E167.bottom")}),-1.0]])]});
            extrude(context, id + "F7", {"entities" : qUnion([Q0]), "operationType" : NewBodyOperationType.REMOVE, "oppositeDirection" : true, "depth" : 1 * mm});
        }
        {
            var Q0;
            Q0=makeQuery(id+"F1.opExtrude","SWEPT_FACE",FACE,{"disambiguationData":[OSD([sQuery(id+"F0.wireOp",EDGE,"E116")])]});
            var sketch = newSketch(context, id + "F8", { "sketchPlane" : qUnion([Q0])});
            skCircle(sketch, "E168", {"center": v(-47.8, 8) * mm, "radius": 4 * mm});
            skSolve(sketch);
        }
        {
            var Q0;
            {var subQ0=sQuery(id+"F8.wireOp",EDGE,"E168");var subQ1=makeQuery(id+"F1.opExtrude","CAP_EDGE",EDGE,{"disambiguationData":[OSD([sQuery(id+"F0.wireOp",EDGE,"E116")])],"isStart":false});var subQ2=makeQuery(id+"F8.imprint","INTERSECT",VERTEX,{"disambiguationData":[OD(0.0)],"derivedFrom":[subQ1,subQ0]});Q0=makeQuery(id+"F8.imprint","IMPRINT",FACE,{"disambiguationData":[TD([[makeQuery(id+"F8.imprint","IMPRINT",EDGE,{"disambiguationData":[TD([[subQ2,1.0]])],"derivedFrom":subQ0}),1.0]])]});}
            extrude(context, id + "F9", {"entities" : qUnion([Q0]), "operationType" : NewBodyOperationType.REMOVE, "endBound" : BoundingType.UP_TO_NEXT, "oppositeDirection" : true, "depth" : 3 * mm});
        }
        {
            var Q0;
            Q0=makeQuery(id+"F1.opExtrude","SWEPT_FACE",FACE,{"disambiguationData":[OSD([sQuery(id+"F0.wireOp",EDGE,"E118")])]});
            var sketch = newSketch(context, id + "F10", { "sketchPlane" : qUnion([Q0])});
            skCircle(sketch, "E169", {"center": v(26.45, 8) * mm, "radius": 4 * mm});
            skSolve(sketch);
        }
        {
            var Q0;
            Q0=makeQuery(id+"F1.opExtrude","SWEPT_FACE",FACE,{"disambiguationData":[OSD([sQuery(id+"F0.wireOp",EDGE,"E6")])]});
            cPlane(context, id + "F11", {"entities" : qUnion([Q0]), "cplaneType" : CPlaneType.OFFSET, "offset" : 9 * mm, "oppositeDirection" : true, "width" : 150 * mm, "height" : 150 * mm});
        }
        {
            var Q0;
            Q0=qCreatedBy(id+"F11.planeOp",FACE);
            var sketch = newSketch(context, id + "F12", { "sketchPlane" : qUnion([Q0])});
            skLineSegment(sketch, "E170.bottom", {"start": v(94.34, 2) * mm, "end": v(84.34, 2) * mm});
            skLineSegment(sketch, "E170.top", {"start": v(94.34, 6) * mm, "end": v(84.34, 6) * mm});
            skLineSegment(sketch, "E170.left", {"start": v(94.34, 2) * mm, "end": v(94.34, 6) * mm});
            skLineSegment(sketch, "E170.right", {"start": v(84.34, 2) * mm, "end": v(84.34, 6) * mm});
            skPoint(sketch, "E170.middle", {"position": v(89.34, 4) * mm});
            skSolve(sketch);
        }
        {
            var Q0;
            Q0 = qSketchRegion(id + "F12", true);
            extrude(context, id + "F13", {"entities" : qUnion([Q0]), "operationType" : NewBodyOperationType.REMOVE, "endBound" : BoundingType.SYMMETRIC, "oppositeDirection" : true, "depth" : 40 * mm});
        }
        {
            var Q0;
            Q0=makeQuery(id+"F1.opExtrude","SWEPT_FACE",FACE,{"disambiguationData":[OSD([sQuery(id+"F0.wireOp",EDGE,"E95.MirrorCS")])]});
            cPlane(context, id + "F14", {"entities" : qUnion([Q0]), "cplaneType" : CPlaneType.OFFSET, "offset" : 9 * mm, "oppositeDirection" : true, "width" : 150 * mm, "height" : 150 * mm});
        }
        {
            var Q0;
            Q0=qCreatedBy(id+"F14.planeOp",FACE);
            var sketch = newSketch(context, id + "F15", { "sketchPlane" : qUnion([Q0])});
            skLineSegment(sketch, "E171.bottom", {"start": v(118.5, 2) * mm, "end": v(108.5, 2) * mm});
            skLineSegment(sketch, "E171.top", {"start": v(118.5, 6) * mm, "end": v(108.5, 6) * mm});
            skLineSegment(sketch, "E171.left", {"start": v(118.5, 2) * mm, "end": v(118.5, 6) * mm});
            skLineSegment(sketch, "E171.right", {"start": v(108.5, 2) * mm, "end": v(108.5, 6) * mm});
            skPoint(sketch, "E171.middle", {"position": v(113.5, 4) * mm});
            skSolve(sketch);
        }
        {
            var Q0;
            Q0=makeQuery(id+"F15.imprint","IMPRINT",FACE,{"disambiguationData":[TD([[makeQuery(id+"F15.imprint","IMPRINT",EDGE,{"derivedFrom":sQuery(id+"F15.wireOp",EDGE,"E171.bottom")}),-1.0]])]});
            extrude(context, id + "F16", {"entities" : qUnion([Q0]), "operationType" : NewBodyOperationType.REMOVE, "endBound" : BoundingType.SYMMETRIC, "oppositeDirection" : true, "depth" : 40 * mm});
        }
        {
            var Q0;
            {var subQ0=sQuery(id+"F15.wireOp",EDGE,"E171.bottom");var subQ1=sQuery(id+"F15.wireOp",EDGE,"E171.right");Q0=makeQuery(id+"F16.boolean.opBoolean","COPY",EDGE,{"disambiguationData":[TD([makeQuery(id+"F1.opExtrude","SWEPT_FACE",FACE,{"disambiguationData":[OSD([sQuery(id+"F0.wireOp",EDGE,"E89.MirrorCS")])]})])],"derivedFrom":makeQuery(id+"F16.opExtrude","SWEPT_EDGE",EDGE,{"disambiguationData":[OSD([subQ0,subQ1])]})});}
            var Q1;
            {var subQ0=sQuery(id+"F15.wireOp",EDGE,"E171.top");var subQ1=sQuery(id+"F15.wireOp",EDGE,"E171.right");Q1=makeQuery(id+"F16.boolean.opBoolean","COPY",EDGE,{"disambiguationData":[TD([makeQuery(id+"F1.opExtrude","SWEPT_FACE",FACE,{"disambiguationData":[OSD([sQuery(id+"F0.wireOp",EDGE,"E89.MirrorCS")])]})])],"derivedFrom":makeQuery(id+"F16.opExtrude","SWEPT_EDGE",EDGE,{"disambiguationData":[OSD([subQ0,subQ1])]})});}
            var Q2;
            {var subQ0=sQuery(id+"F15.wireOp",EDGE,"E171.top");var subQ1=sQuery(id+"F15.wireOp",EDGE,"E171.left");Q2=makeQuery(id+"F16.boolean.opBoolean","COPY",EDGE,{"disambiguationData":[TD([makeQuery(id+"F1.opExtrude","SWEPT_FACE",FACE,{"disambiguationData":[OSD([sQuery(id+"F0.wireOp",EDGE,"E89.MirrorCS")])]})])],"derivedFrom":makeQuery(id+"F16.opExtrude","SWEPT_EDGE",EDGE,{"disambiguationData":[OSD([subQ0,subQ1])]})});}
            var Q3;
            {var subQ0=sQuery(id+"F15.wireOp",EDGE,"E171.bottom");var subQ1=sQuery(id+"F15.wireOp",EDGE,"E171.left");Q3=makeQuery(id+"F16.boolean.opBoolean","COPY",EDGE,{"disambiguationData":[TD([makeQuery(id+"F1.opExtrude","SWEPT_FACE",FACE,{"disambiguationData":[OSD([sQuery(id+"F0.wireOp",EDGE,"E89.MirrorCS")])]})])],"derivedFrom":makeQuery(id+"F16.opExtrude","SWEPT_EDGE",EDGE,{"disambiguationData":[OSD([subQ0,subQ1])]})});}
            var Q4;
            {var subQ0=sQuery(id+"F15.wireOp",EDGE,"E171.left");var subQ1=sQuery(id+"F15.wireOp",EDGE,"E171.bottom");Q4=makeQuery(id+"F16.boolean.opBoolean","COPY",EDGE,{"disambiguationData":[TD([makeQuery(id+"F1.opExtrude","SWEPT_FACE",FACE,{"disambiguationData":[OSD([sQuery(id+"F0.wireOp",EDGE,"E86.MirrorCS")])]})])],"derivedFrom":makeQuery(id+"F16.opExtrude","SWEPT_EDGE",EDGE,{"disambiguationData":[OSD([subQ1,subQ0])]})});}
            var Q5;
            {var subQ0=sQuery(id+"F15.wireOp",EDGE,"E171.bottom");var subQ1=sQuery(id+"F15.wireOp",EDGE,"E171.right");Q5=makeQuery(id+"F16.boolean.opBoolean","COPY",EDGE,{"disambiguationData":[TD([makeQuery(id+"F1.opExtrude","SWEPT_FACE",FACE,{"disambiguationData":[OSD([sQuery(id+"F0.wireOp",EDGE,"E86.MirrorCS")])]})])],"derivedFrom":makeQuery(id+"F16.opExtrude","SWEPT_EDGE",EDGE,{"disambiguationData":[OSD([subQ0,subQ1])]})});}
            var Q6;
            {var subQ0=sQuery(id+"F15.wireOp",EDGE,"E171.top");var subQ1=sQuery(id+"F15.wireOp",EDGE,"E171.right");Q6=makeQuery(id+"F16.boolean.opBoolean","COPY",EDGE,{"disambiguationData":[TD([makeQuery(id+"F1.opExtrude","SWEPT_FACE",FACE,{"disambiguationData":[OSD([sQuery(id+"F0.wireOp",EDGE,"E86.MirrorCS")])]})])],"derivedFrom":makeQuery(id+"F16.opExtrude","SWEPT_EDGE",EDGE,{"disambiguationData":[OSD([subQ0,subQ1])]})});}
            var Q7;
            {var subQ0=sQuery(id+"F15.wireOp",EDGE,"E171.top");var subQ1=sQuery(id+"F15.wireOp",EDGE,"E171.left");Q7=makeQuery(id+"F16.boolean.opBoolean","COPY",EDGE,{"disambiguationData":[TD([makeQuery(id+"F1.opExtrude","SWEPT_FACE",FACE,{"disambiguationData":[OSD([sQuery(id+"F0.wireOp",EDGE,"E86.MirrorCS")])]})])],"derivedFrom":makeQuery(id+"F16.opExtrude","SWEPT_EDGE",EDGE,{"disambiguationData":[OSD([subQ0,subQ1])]})});}
            var Q8;
            {var subQ0=sQuery(id+"F12.wireOp",EDGE,"E170.right");var subQ1=sQuery(id+"F12.wireOp",EDGE,"E170.top");Q8=makeQuery(id+"FrttgUIXkOwAJPR_1.1.F13.boolean.opBoolean","COPY",EDGE,{"disambiguationData":[TD([makeQuery(id+"F1.opExtrude","SWEPT_FACE",FACE,{"disambiguationData":[OSD([sQuery(id+"F0.wireOp",EDGE,"E79.MirrorCS")])]})])],"derivedFrom":makeQuery(id+"FrttgUIXkOwAJPR_1.1.F13.opExtrude","SWEPT_EDGE",EDGE,{"disambiguationData":[OSD([subQ1,subQ0])]})});}
            var Q9;
            {var subQ0=sQuery(id+"F12.wireOp",EDGE,"E170.bottom");var subQ1=sQuery(id+"F12.wireOp",EDGE,"E170.right");Q9=makeQuery(id+"FrttgUIXkOwAJPR_1.1.F13.boolean.opBoolean","COPY",EDGE,{"disambiguationData":[TD([makeQuery(id+"F1.opExtrude","SWEPT_FACE",FACE,{"disambiguationData":[OSD([sQuery(id+"F0.wireOp",EDGE,"E79.MirrorCS")])]})])],"derivedFrom":makeQuery(id+"FrttgUIXkOwAJPR_1.1.F13.opExtrude","SWEPT_EDGE",EDGE,{"disambiguationData":[OSD([subQ0,subQ1])]})});}
            var Q10;
            {var subQ0=sQuery(id+"F12.wireOp",EDGE,"E170.bottom");var subQ1=sQuery(id+"F12.wireOp",EDGE,"E170.right");Q10=makeQuery(id+"FrttgUIXkOwAJPR_1.1.F13.boolean.opBoolean","COPY",EDGE,{"disambiguationData":[TD([makeQuery(id+"F1.opExtrude","SWEPT_FACE",FACE,{"disambiguationData":[OSD([sQuery(id+"F0.wireOp",EDGE,"E87.MirrorCS")])]})])],"derivedFrom":makeQuery(id+"FrttgUIXkOwAJPR_1.1.F13.opExtrude","SWEPT_EDGE",EDGE,{"disambiguationData":[OSD([subQ0,subQ1])]})});}
            var Q11;
            {var subQ0=sQuery(id+"F12.wireOp",EDGE,"E170.bottom");var subQ1=sQuery(id+"F12.wireOp",EDGE,"E170.left");Q11=makeQuery(id+"FrttgUIXkOwAJPR_1.1.F13.boolean.opBoolean","COPY",EDGE,{"disambiguationData":[TD([makeQuery(id+"F1.opExtrude","SWEPT_FACE",FACE,{"disambiguationData":[OSD([sQuery(id+"F0.wireOp",EDGE,"E79.MirrorCS")])]})])],"derivedFrom":makeQuery(id+"FrttgUIXkOwAJPR_1.1.F13.opExtrude","SWEPT_EDGE",EDGE,{"disambiguationData":[OSD([subQ0,subQ1])]})});}
            var Q12;
            {var subQ0=sQuery(id+"F12.wireOp",EDGE,"E170.top");var subQ1=sQuery(id+"F12.wireOp",EDGE,"E170.left");Q12=makeQuery(id+"FrttgUIXkOwAJPR_1.1.F13.boolean.opBoolean","COPY",EDGE,{"disambiguationData":[TD([makeQuery(id+"F1.opExtrude","SWEPT_FACE",FACE,{"disambiguationData":[OSD([sQuery(id+"F0.wireOp",EDGE,"E79.MirrorCS")])]})])],"derivedFrom":makeQuery(id+"FrttgUIXkOwAJPR_1.1.F13.opExtrude","SWEPT_EDGE",EDGE,{"disambiguationData":[OSD([subQ0,subQ1])]})});}
            var Q13;
            {var subQ0=sQuery(id+"F12.wireOp",EDGE,"E170.top");var subQ1=sQuery(id+"F12.wireOp",EDGE,"E170.left");Q13=makeQuery(id+"FrttgUIXkOwAJPR_1.1.F13.boolean.opBoolean","COPY",EDGE,{"disambiguationData":[TD([makeQuery(id+"F1.opExtrude","SWEPT_FACE",FACE,{"disambiguationData":[OSD([sQuery(id+"F0.wireOp",EDGE,"E87.MirrorCS")])]})])],"derivedFrom":makeQuery(id+"FrttgUIXkOwAJPR_1.1.F13.opExtrude","SWEPT_EDGE",EDGE,{"disambiguationData":[OSD([subQ0,subQ1])]})});}
            var Q14;
            {var subQ0=sQuery(id+"F12.wireOp",EDGE,"E170.bottom");var subQ1=sQuery(id+"F12.wireOp",EDGE,"E170.left");Q14=makeQuery(id+"FrttgUIXkOwAJPR_1.1.F13.boolean.opBoolean","COPY",EDGE,{"disambiguationData":[TD([makeQuery(id+"F1.opExtrude","SWEPT_FACE",FACE,{"disambiguationData":[OSD([sQuery(id+"F0.wireOp",EDGE,"E87.MirrorCS")])]})])],"derivedFrom":makeQuery(id+"FrttgUIXkOwAJPR_1.1.F13.opExtrude","SWEPT_EDGE",EDGE,{"disambiguationData":[OSD([subQ0,subQ1])]})});}
            var Q15;
            {var subQ0=sQuery(id+"F12.wireOp",EDGE,"E170.right");var subQ1=sQuery(id+"F12.wireOp",EDGE,"E170.top");Q15=makeQuery(id+"FrttgUIXkOwAJPR_1.1.F13.boolean.opBoolean","COPY",EDGE,{"disambiguationData":[TD([makeQuery(id+"F1.opExtrude","SWEPT_FACE",FACE,{"disambiguationData":[OSD([sQuery(id+"F0.wireOp",EDGE,"E87.MirrorCS")])]})])],"derivedFrom":makeQuery(id+"FrttgUIXkOwAJPR_1.1.F13.opExtrude","SWEPT_EDGE",EDGE,{"disambiguationData":[OSD([subQ1,subQ0])]})});}
            var Q16;
            {var subQ0=sQuery(id+"F15.wireOp",EDGE,"E171.bottom");var subQ1=sQuery(id+"F15.wireOp",EDGE,"E171.right");Q16=makeQuery(id+"FyABKiLMpsOIMja_1.1.F16.boolean.opBoolean","COPY",EDGE,{"disambiguationData":[TD([makeQuery(id+"F1.opExtrude","SWEPT_FACE",FACE,{"disambiguationData":[OSD([sQuery(id+"F0.wireOp",EDGE,"E32.trimOffspring")])]})])],"derivedFrom":makeQuery(id+"FyABKiLMpsOIMja_1.1.F16.opExtrude","SWEPT_EDGE",EDGE,{"disambiguationData":[OSD([subQ0,subQ1])]})});}
            var Q17;
            {var subQ0=sQuery(id+"F15.wireOp",EDGE,"E171.bottom");var subQ1=sQuery(id+"F15.wireOp",EDGE,"E171.right");Q17=makeQuery(id+"FyABKiLMpsOIMja_1.1.F16.boolean.opBoolean","COPY",EDGE,{"disambiguationData":[TD([makeQuery(id+"F1.opExtrude","SWEPT_FACE",FACE,{"disambiguationData":[OSD([sQuery(id+"F0.wireOp",EDGE,"E4")])]})])],"derivedFrom":makeQuery(id+"FyABKiLMpsOIMja_1.1.F16.opExtrude","SWEPT_EDGE",EDGE,{"disambiguationData":[OSD([subQ0,subQ1])]})});}
            var Q18;
            {var subQ0=sQuery(id+"F15.wireOp",EDGE,"E171.bottom");var subQ1=sQuery(id+"F15.wireOp",EDGE,"E171.left");Q18=makeQuery(id+"FyABKiLMpsOIMja_1.1.F16.boolean.opBoolean","COPY",EDGE,{"disambiguationData":[TD([makeQuery(id+"F1.opExtrude","SWEPT_FACE",FACE,{"disambiguationData":[OSD([sQuery(id+"F0.wireOp",EDGE,"E32.trimOffspring")])]})])],"derivedFrom":makeQuery(id+"FyABKiLMpsOIMja_1.1.F16.opExtrude","SWEPT_EDGE",EDGE,{"disambiguationData":[OSD([subQ0,subQ1])]})});}
            var Q19;
            {var subQ0=sQuery(id+"F15.wireOp",EDGE,"E171.top");var subQ1=sQuery(id+"F15.wireOp",EDGE,"E171.left");Q19=makeQuery(id+"FyABKiLMpsOIMja_1.1.F16.boolean.opBoolean","COPY",EDGE,{"disambiguationData":[TD([makeQuery(id+"F1.opExtrude","SWEPT_FACE",FACE,{"disambiguationData":[OSD([sQuery(id+"F0.wireOp",EDGE,"E32.trimOffspring")])]})])],"derivedFrom":makeQuery(id+"FyABKiLMpsOIMja_1.1.F16.opExtrude","SWEPT_EDGE",EDGE,{"disambiguationData":[OSD([subQ0,subQ1])]})});}
            var Q20;
            {var subQ0=sQuery(id+"F15.wireOp",EDGE,"E171.top");var subQ1=sQuery(id+"F15.wireOp",EDGE,"E171.right");Q20=makeQuery(id+"FyABKiLMpsOIMja_1.1.F16.boolean.opBoolean","COPY",EDGE,{"disambiguationData":[TD([makeQuery(id+"F1.opExtrude","SWEPT_FACE",FACE,{"disambiguationData":[OSD([sQuery(id+"F0.wireOp",EDGE,"E32.trimOffspring")])]})])],"derivedFrom":makeQuery(id+"FyABKiLMpsOIMja_1.1.F16.opExtrude","SWEPT_EDGE",EDGE,{"disambiguationData":[OSD([subQ0,subQ1])]})});}
            var Q21;
            {var subQ0=sQuery(id+"F12.wireOp",EDGE,"E170.top");var subQ1=sQuery(id+"F12.wireOp",EDGE,"E170.left");Q21=makeQuery(id+"F13.boolean.opBoolean","COPY",EDGE,{"disambiguationData":[TD([makeQuery(id+"F1.opExtrude","SWEPT_FACE",FACE,{"disambiguationData":[OSD([sQuery(id+"F0.wireOp",EDGE,"E29.trimOffspring")])]})])],"derivedFrom":makeQuery(id+"F13.opExtrude","SWEPT_EDGE",EDGE,{"disambiguationData":[OSD([subQ0,subQ1])]})});}
            var Q22;
            {var subQ0=sQuery(id+"F12.wireOp",EDGE,"E170.top");var subQ1=sQuery(id+"F12.wireOp",EDGE,"E170.left");Q22=makeQuery(id+"F13.boolean.opBoolean","COPY",EDGE,{"disambiguationData":[TD([makeQuery(id+"F1.opExtrude","SWEPT_FACE",FACE,{"disambiguationData":[OSD([sQuery(id+"F0.wireOp",EDGE,"E3")])]})])],"derivedFrom":makeQuery(id+"F13.opExtrude","SWEPT_EDGE",EDGE,{"disambiguationData":[OSD([subQ0,subQ1])]})});}
            var Q23;
            {var subQ0=sQuery(id+"F12.wireOp",EDGE,"E170.right");var subQ1=sQuery(id+"F12.wireOp",EDGE,"E170.top");Q23=makeQuery(id+"F13.boolean.opBoolean","COPY",EDGE,{"disambiguationData":[TD([makeQuery(id+"F1.opExtrude","SWEPT_FACE",FACE,{"disambiguationData":[OSD([sQuery(id+"F0.wireOp",EDGE,"E3")])]})])],"derivedFrom":makeQuery(id+"F13.opExtrude","SWEPT_EDGE",EDGE,{"disambiguationData":[OSD([subQ1,subQ0])]})});}
            var Q24;
            {var subQ0=sQuery(id+"F12.wireOp",EDGE,"E170.top");var subQ1=sQuery(id+"F12.wireOp",EDGE,"E170.right");Q24=makeQuery(id+"F13.boolean.opBoolean","COPY",EDGE,{"disambiguationData":[TD([makeQuery(id+"F1.opExtrude","SWEPT_FACE",FACE,{"disambiguationData":[OSD([sQuery(id+"F0.wireOp",EDGE,"E29.trimOffspring")])]})])],"derivedFrom":makeQuery(id+"F13.opExtrude","SWEPT_EDGE",EDGE,{"disambiguationData":[OSD([subQ0,subQ1])]})});}
            var Q25;
            {var subQ0=sQuery(id+"F12.wireOp",EDGE,"E170.bottom");var subQ1=sQuery(id+"F12.wireOp",EDGE,"E170.right");Q25=makeQuery(id+"F13.boolean.opBoolean","COPY",EDGE,{"disambiguationData":[TD([makeQuery(id+"F1.opExtrude","SWEPT_FACE",FACE,{"disambiguationData":[OSD([sQuery(id+"F0.wireOp",EDGE,"E3")])]})])],"derivedFrom":makeQuery(id+"F13.opExtrude","SWEPT_EDGE",EDGE,{"disambiguationData":[OSD([subQ0,subQ1])]})});}
            var Q26;
            {var subQ0=sQuery(id+"F12.wireOp",EDGE,"E170.bottom");var subQ1=sQuery(id+"F12.wireOp",EDGE,"E170.right");Q26=makeQuery(id+"F13.boolean.opBoolean","COPY",EDGE,{"disambiguationData":[TD([makeQuery(id+"F1.opExtrude","SWEPT_FACE",FACE,{"disambiguationData":[OSD([sQuery(id+"F0.wireOp",EDGE,"E29.trimOffspring")])]})])],"derivedFrom":makeQuery(id+"F13.opExtrude","SWEPT_EDGE",EDGE,{"disambiguationData":[OSD([subQ0,subQ1])]})});}
            var Q27;
            {var subQ0=sQuery(id+"F12.wireOp",EDGE,"E170.bottom");var subQ1=sQuery(id+"F12.wireOp",EDGE,"E170.left");Q27=makeQuery(id+"F13.boolean.opBoolean","COPY",EDGE,{"disambiguationData":[TD([makeQuery(id+"F1.opExtrude","SWEPT_FACE",FACE,{"disambiguationData":[OSD([sQuery(id+"F0.wireOp",EDGE,"E29.trimOffspring")])]})])],"derivedFrom":makeQuery(id+"F13.opExtrude","SWEPT_EDGE",EDGE,{"disambiguationData":[OSD([subQ0,subQ1])]})});}
            var Q28;
            {var subQ0=sQuery(id+"F12.wireOp",EDGE,"E170.bottom");var subQ1=sQuery(id+"F12.wireOp",EDGE,"E170.left");Q28=makeQuery(id+"F13.boolean.opBoolean","COPY",EDGE,{"disambiguationData":[TD([makeQuery(id+"F1.opExtrude","SWEPT_FACE",FACE,{"disambiguationData":[OSD([sQuery(id+"F0.wireOp",EDGE,"E3")])]})])],"derivedFrom":makeQuery(id+"F13.opExtrude","SWEPT_EDGE",EDGE,{"disambiguationData":[OSD([subQ0,subQ1])]})});}
            var Q29;
            {var subQ0=sQuery(id+"F15.wireOp",EDGE,"E171.left");var subQ1=sQuery(id+"F15.wireOp",EDGE,"E171.top");Q29=makeQuery(id+"FyABKiLMpsOIMja_1.1.F16.boolean.opBoolean","COPY",EDGE,{"disambiguationData":[TD([makeQuery(id+"F1.opExtrude","SWEPT_FACE",FACE,{"disambiguationData":[OSD([sQuery(id+"F0.wireOp",EDGE,"E4")])]})])],"derivedFrom":makeQuery(id+"FyABKiLMpsOIMja_1.1.F16.opExtrude","SWEPT_EDGE",EDGE,{"disambiguationData":[OSD([subQ1,subQ0])]})});}
            var Q30;
            {var subQ0=sQuery(id+"F15.wireOp",EDGE,"E171.top");var subQ1=sQuery(id+"F15.wireOp",EDGE,"E171.right");Q30=makeQuery(id+"FyABKiLMpsOIMja_1.1.F16.boolean.opBoolean","COPY",EDGE,{"disambiguationData":[TD([makeQuery(id+"F1.opExtrude","SWEPT_FACE",FACE,{"disambiguationData":[OSD([sQuery(id+"F0.wireOp",EDGE,"E4")])]})])],"derivedFrom":makeQuery(id+"FyABKiLMpsOIMja_1.1.F16.opExtrude","SWEPT_EDGE",EDGE,{"disambiguationData":[OSD([subQ0,subQ1])]})});}
            var Q31;
            {var subQ0=sQuery(id+"F15.wireOp",EDGE,"E171.left");var subQ1=sQuery(id+"F15.wireOp",EDGE,"E171.bottom");Q31=makeQuery(id+"FyABKiLMpsOIMja_1.1.F16.boolean.opBoolean","COPY",EDGE,{"disambiguationData":[TD([makeQuery(id+"F1.opExtrude","SWEPT_FACE",FACE,{"disambiguationData":[OSD([sQuery(id+"F0.wireOp",EDGE,"E4")])]})])],"derivedFrom":makeQuery(id+"FyABKiLMpsOIMja_1.1.F16.opExtrude","SWEPT_EDGE",EDGE,{"disambiguationData":[OSD([subQ1,subQ0])]})});}
            fillet(context, id + "F17", {"entities" : qUnion([Q0, Q1, Q2, Q3, Q4, Q5, Q6, Q7, Q8, Q9, Q10, Q11, Q12, Q13, Q14, Q15, Q16, Q17, Q18, Q19, Q20, Q21, Q22, Q23, Q24, Q25, Q26, Q27, Q28, Q29, Q30, Q31]), "radius" : 2 * mm, "tangentPropagation" : true, "allowEdgeOverflow" : false});
        }
        {
            var Q0;
            {var subQ0=sQuery(id+"F10.wireOp",EDGE,"E169");var subQ1=makeQuery(id+"F1.opExtrude","CAP_EDGE",EDGE,{"disambiguationData":[OSD([sQuery(id+"F0.wireOp",EDGE,"E118")])],"isStart":false});var subQ2=makeQuery(id+"F10.imprint","INTERSECT",VERTEX,{"disambiguationData":[OD(0.0)],"derivedFrom":[subQ1,subQ0]});Q0=makeQuery(id+"F10.imprint","IMPRINT",FACE,{"disambiguationData":[TD([[makeQuery(id+"F10.imprint","IMPRINT",EDGE,{"disambiguationData":[TD([[subQ2,1.0]])],"derivedFrom":subQ0}),1.0]])]});}
            extrude(context, id + "F18", {"entities" : qUnion([Q0]), "operationType" : NewBodyOperationType.REMOVE, "endBound" : BoundingType.UP_TO_NEXT, "oppositeDirection" : true, "depth" : 25 * mm});
        }
    });
